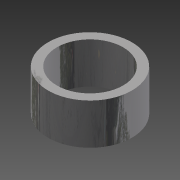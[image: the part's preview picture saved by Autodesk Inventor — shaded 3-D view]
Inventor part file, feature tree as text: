
AUTODESK INVENTOR PART (.ipt)
format: ipt  version: 2015 (Build 190159000, 159)  size: 107,008 bytes
history: native  units: mm
features: sketch x2, other x1, extrude x1, hole x1
ambient origin geometry x8: Origin, YZ Plane, XZ Plane, XY Plane, X Axis, Y Axis, Z Axis, Center Point
bodies: Body1 (feature_tree)
feature tree (5):
  other  "Bryła1"
  extrude  "Wyciągnięcie proste1"  Depth=17.2mm
  hole  "Otwór1"  [1 undecoded]
  sketch  "Szkic1"
  sketch  "Szkic2"
note: 1 required parameter value undecoded (feature->parameter linkage not recoverable at this tier; creation-order binding heuristic only, values carry confidence <= 0.55)
